# Revit family: HVAC_Mechanical-Ventilation_Ice-Air_FCU_Hi-Rise
name_source: partatom
category: Mechanical Equipment
revit_build: Autodesk Revit 2015 (Build: 20140606_1530(x64)
units: mm (PartAtom-declared; Revit-internal decimal feet)

## types (6) — shared parameters
Aluminum Material = Aluminum - Ice_Air - White
BIMobject category = Air Conditioning
BIMobject category code = hvac-air-con
BIMobject main category = HVAC
BIMobject main category code = hvac
Brand url = http://www.ice-air.com
Condensate Connection = 0.5 "
Control Panel Height = 60 "
Default Elevation = 48 "
Description = ICE AIR Fan Coil Hi Rise Units are designed specifically for high-rise installations – apartments, hotels, condominiums and office buildings.
Design country = United States
Display Material = LED - Ice_Air - Blue
Edition number = 1
Floor Offset = 5 "
Frequency = 60 Hz
Front Panel Height = 54 "
Height = 88 "
IFC Classification = Heat Exchanger
Inlet/Outlet Connection = 0.5 "
Manufacturer = Ice Air
Manufacturer country = United States
Manufacturer name = Ice Air
Masterformat 2014 Code = 23 82 19
Masterformat 2014 Description = Fan Coil Units
Motor = 115V/60Hz
NBS Reference Code = 65-00-29
NBS Reference Description = Fan Coil Units
OmniClass Code = 23-33 33 11
OmniClass Description = Fan Coil Units
Plastic Material = Plastic - Ice_Air - White
Product Guid = a8049a33-25b6-41cd-9a2c-2f6981b895a3
Product SKU = hi-rise-fan-coil-unit
Product data url = https://bimobject.com
Product family = FCU
Product group = Hi-Rise
Product url = http://www.ice-air.com
QR code = http://bimobject.com
Steel Material = Steel - Ice_Air - Galvanized
Technical description = http://www.ice-air.com
UNSPSC Code = 4010
URL = http://www.ice-air.com
Uniclass 1.4 Code = JU84
Uniclass 1.4 Description = Heating and cooling coils
Uniclass 2.0 Code = PR-65-00-29
Uniclass 2.0 Description = Fan Coil Units
Uniclass 2015 Code = Pr_60_65_37
Uniclass 2015 Name = Heating and cooling coils
Uniformat II Code = D3090
Uniformat II Description = Other HVAC Systems & Equipment
Voltage = 115 V
Weight Net (Kg) = 0
z 2-pipe = Pipe System : 2-pipe
z 4-pipe = Pipe System : 4-pipe
zero-valued in all types: Nominal height, Nominal width

## per-type parameters (varying)
| type | Air Flow (High) | Air Flow (Low) | Air Flow (Med) | Cooling Capacity (High) | Cooling Capacity (Low) | Cooling Capacity (Med) | Depth | Discharge Height | Discharge Width | Double Supply | Heating Capacity (High) | Heating Capacity (Low) | Heating Capacity (Med) | Single Supply | Top Duct Height | Top Duct Width | Width | z Type |
| 5FCHR03 | 300 CFM | 150 CFM | 225 CFM | 11500.0 Btu/h | 6900.0 Btu/h | 8625.0 Btu/h | 17 " | 8 " | 14 " | No | 17250.0 Btu/h | 10350.0 Btu/h | 12900.0 Btu/h | Yes | 10 " | 14 " | 17 " | 1 |
| 5FCHR04 | 400 CFM | 200 CFM | 300 CFM | 13600.0 Btu/h | 8160.0 Btu/h | 10200.0 Btu/h | 17 " | 12 " | 14 " | No | 20400.0 Btu/h | 12250.0 Btu/h | 15300.0 Btu/h | Yes | 10 " | 14 " | 17 " | 2 |
| 5FCHR06 | 600 CFM | 300 CFM | 450 CFM | 21900.0 Btu/h | 13140.0 Btu/h | 16425.0 Btu/h | 20 " | 10 " | 18 " | No | 32850.0 Btu/h | 19700.0 Btu/h | 24600.0 Btu/h | Yes | 12 " | 16 " | 20 " | 3 |
| 5FCHR08 | 800 CFM | 400 CFM | 600 CFM | 27500.0 Btu/h | 16500.0 Btu/h | 20625.0 Btu/h | 20 " | 12 " | 18 " | No | 41250.0 Btu/h | 24750.0 Btu/h | 30900.0 Btu/h | Yes | 12 " | 16 " | 20 " | 4 |
| 5FCHR10 | 1000 CFM | 500 CFM | 750 CFM | 37700.0 Btu/h | 22620.0 Btu/h | 28275.0 Btu/h | 24 " | 8 " | 22 " | Yes | 56550.0 Btu/h | 33950.0 Btu/h | 42400.0 Btu/h | No | 16 " | 18 " | 24 " | 5 |
| 5FCHR12 | 1200 CFM | 600 CFM | 900 CFM | 43100.0 Btu/h | 25860.0 Btu/h | 32325.0 Btu/h | 24 " | 8 " | 22 " | Yes | 64650.0 Btu/h | 38750.0 Btu/h | 48450.0 Btu/h | No | 16 " | 18 " | 24 " | 6 |

note: column(s) folded — value = type name in every type: Model

## geometry (parser evidence)
native form markers: Sweep x9
no freeform markers — native parametric forms only
